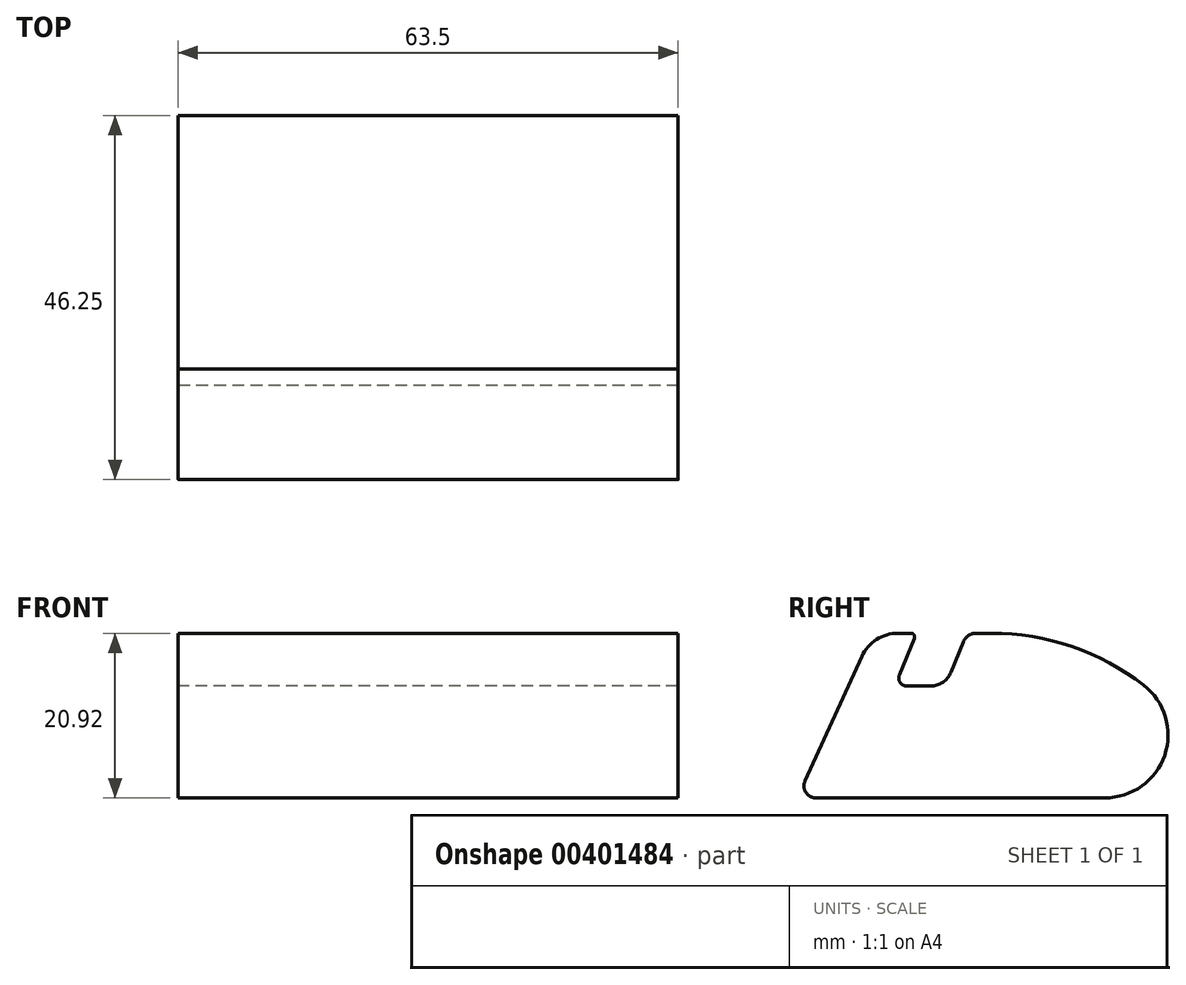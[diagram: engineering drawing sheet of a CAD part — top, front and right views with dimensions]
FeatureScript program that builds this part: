
annotation { "Feature Type Name" : "Feature", "Feature Type Description" : "" }
export const myFeature = defineFeature(function(context is Context, id is Id, definition is map)
    precondition{}
    {
        {
            var Q0;
            Q0=qCreatedBy(makeId("Right.planeOp"),FACE);
            var sketch = newSketch(context, id + "F0", { "sketchPlane" : qUnion([Q0])});
            skLineSegment(sketch, "E0", {"start": v(-26.45, 0) * mm, "end": v(27.97, 0) * mm});
            skLineSegment(sketch, "E1", {"start": v(27.97, 0) * mm, "end": v(27.97, 20.92) * mm});
            skLineSegment(sketch, "E2", {"start": v(27.97, 20.92) * mm, "end": v(-4.92, 20.92) * mm});
            skLineSegment(sketch, "E3", {"start": v(-4.92, 20.92) * mm, "end": v(-7.66, 14.22) * mm});
            skLineSegment(sketch, "E4", {"start": v(-7.66, 14.22) * mm, "end": v(-14.05, 14.22) * mm});
            skLineSegment(sketch, "E5", {"start": v(-14.05, 14.22) * mm, "end": v(-14.05, 14.22) * mm});
            skLineSegment(sketch, "E6", {"start": v(-14.05, 14.22) * mm, "end": v(-11.3, 20.92) * mm});
            skLineSegment(sketch, "E7", {"start": v(-11.3, 20.92) * mm, "end": v(-16.9, 20.92) * mm});
            skLineSegment(sketch, "E8", {"start": v(-16.9, 20.92) * mm, "end": v(-26.45, 0) * mm});
            skSolve(sketch);
        }
        {
            var Q0;
            Q0=makeQuery(id+"F0.imprint","IMPRINT",FACE,{"disambiguationData":[TD([[makeQuery(id+"F0.imprint","IMPRINT",EDGE,{"derivedFrom":sQuery(id+"F0.wireOp",EDGE,"E0")}),1.0]])]});
            extrude(context, id + "F1", {"entities" : qUnion([Q0]), "depth" : 63.5 * mm});
        }
        {
            var Q0;
            Q0=makeQuery(id+"F1.opExtrude","SWEPT_EDGE",EDGE,{"disambiguationData":[OSD([sQuery(id+"F0.wireOp",EDGE,"E2"),sQuery(id+"F0.wireOp",EDGE,"E3")])]});
            fillet(context, id + "F2", {"entities" : qUnion([Q0]), "radius" : 1.8 * mm, "tangentPropagation" : true, "allowEdgeOverflow" : false});
        }
        {
            var Q0;
            Q0=makeQuery(id+"F1.opExtrude","SWEPT_EDGE",EDGE,{"disambiguationData":[OSD([sQuery(id+"F0.wireOp",EDGE,"E6"),sQuery(id+"F0.wireOp",EDGE,"E7")])]});
            fillet(context, id + "F3", {"entities" : qUnion([Q0]), "radius" : 0.48 * mm, "tangentPropagation" : true, "allowEdgeOverflow" : false});
        }
        {
            var Q0;
            Q0=makeQuery(id+"F1.opExtrude","SWEPT_EDGE",EDGE,{"disambiguationData":[OSD([sQuery(id+"F0.wireOp",EDGE,"E3"),sQuery(id+"F0.wireOp",EDGE,"E4")])]});
            fillet(context, id + "F4", {"entities" : qUnion([Q0]), "radius" : 2.73 * mm, "tangentPropagation" : true, "allowEdgeOverflow" : false});
        }
        {
            var Q0;
            Q0=makeQuery(id+"F1.opExtrude","SWEPT_EDGE",EDGE,{"disambiguationData":[OSD([sQuery(id+"F0.wireOp",EDGE,"E4"),sQuery(id+"F0.wireOp",EDGE,"E6")])]});
            fillet(context, id + "F5", {"entities" : qUnion([Q0]), "radius" : 1 * mm, "tangentPropagation" : true, "allowEdgeOverflow" : false});
        }
        {
            var Q0;
            Q0=makeQuery(id+"F1.opExtrude","SWEPT_EDGE",EDGE,{"disambiguationData":[OSD([sQuery(id+"F0.wireOp",EDGE,"E7"),sQuery(id+"F0.wireOp",EDGE,"E8")])]});
            fillet(context, id + "F6", {"entities" : qUnion([Q0]), "radius" : 5.08 * mm, "tangentPropagation" : true, "allowEdgeOverflow" : false});
        }
        {
            var Q0;
            Q0=makeQuery(id+"F1.opExtrude","SWEPT_EDGE",EDGE,{"disambiguationData":[OSD([sQuery(id+"F0.wireOp",EDGE,"E0"),sQuery(id+"F0.wireOp",EDGE,"E8")])]});
            fillet(context, id + "F7", {"entities" : qUnion([Q0]), "radius" : 1.52 * mm, "tangentPropagation" : true, "allowEdgeOverflow" : false});
        }
        {
            var Q0;
            Q0=makeQuery(id+"F1.opExtrude","SWEPT_EDGE",EDGE,{"disambiguationData":[OSD([sQuery(id+"F0.wireOp",EDGE,"E1"),sQuery(id+"F0.wireOp",EDGE,"E2")])]});
            fillet(context, id + "F8", {"entities" : qUnion([Q0]), "radius" : 31.63 * mm, "tangentPropagation" : true, "allowEdgeOverflow" : false});
        }
        {
            var Q0;
            Q0=makeQuery(id+"F8.opFillet","BLEND_EDGE",EDGE,{"blendedFrom":[makeQuery(id+"F1.opExtrude","SWEPT_EDGE",EDGE,{"disambiguationData":[OSD([sQuery(id+"F0.wireOp",EDGE,"E1"),sQuery(id+"F0.wireOp",EDGE,"E2")])]}),makeQuery(id+"F1.opExtrude","SWEPT_FACE",FACE,{"disambiguationData":[OSD([sQuery(id+"F0.wireOp",EDGE,"E0")])]})],"blendedInto":[makeQuery(id+"F1.opExtrude","SWEPT_FACE",FACE,{"disambiguationData":[OSD([sQuery(id+"F0.wireOp",EDGE,"E0")])]})]});
            fillet(context, id + "F9", {"entities" : qUnion([Q0]), "radius" : 8 * mm, "tangentPropagation" : true, "allowEdgeOverflow" : false});
        }
    });
